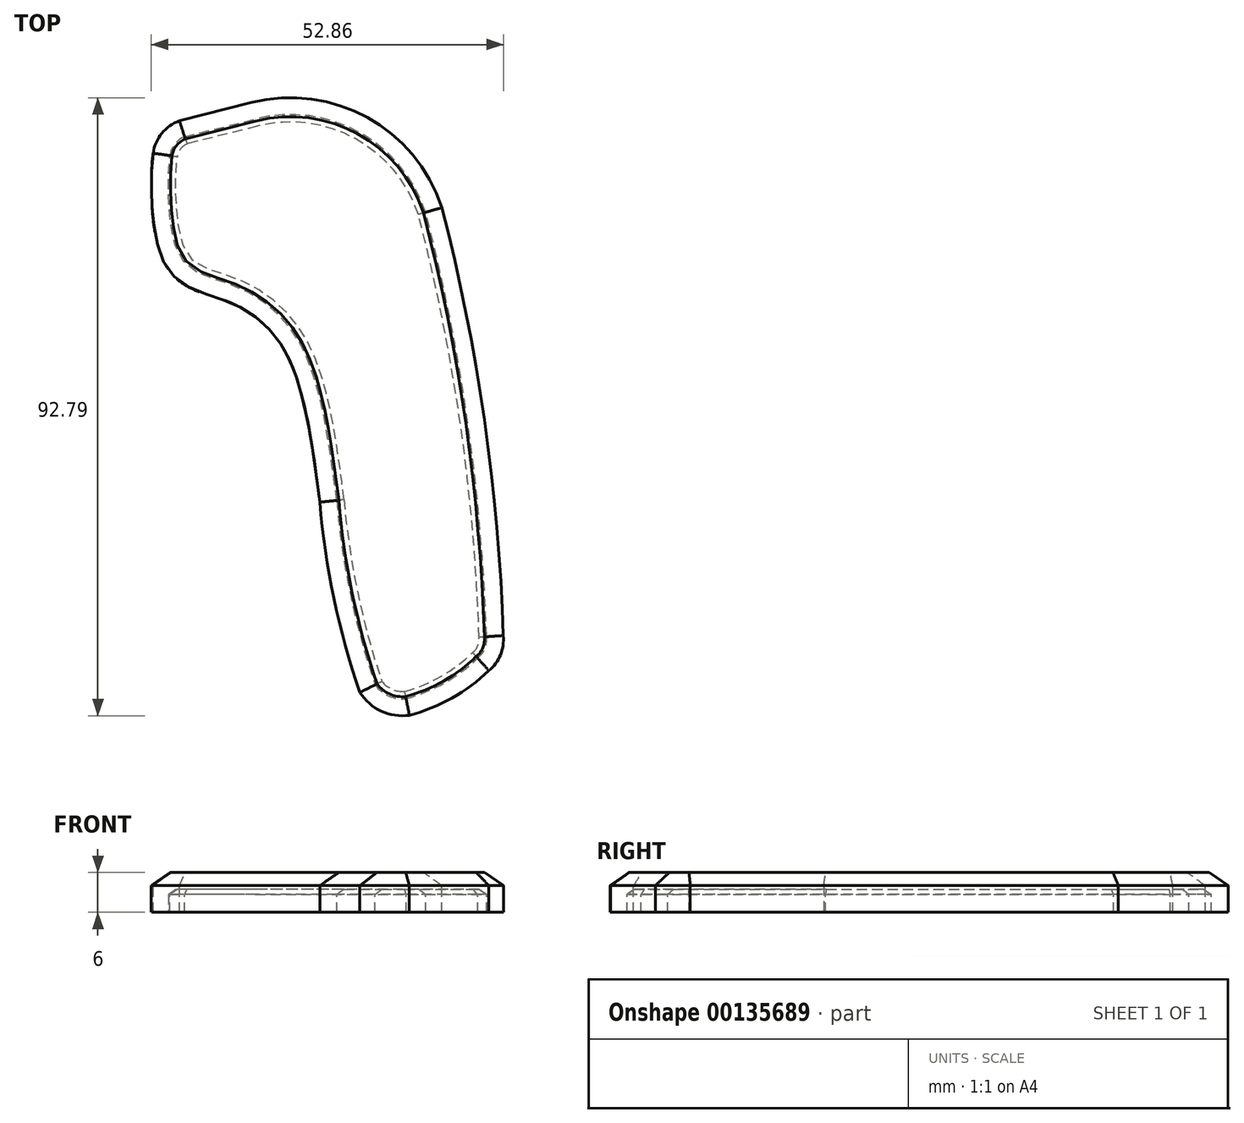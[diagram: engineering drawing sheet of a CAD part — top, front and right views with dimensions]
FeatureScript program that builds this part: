
annotation { "Feature Type Name" : "Feature", "Feature Type Description" : "" }
export const myFeature = defineFeature(function(context is Context, id is Id, definition is map)
    precondition{}
    {
        {
            var Q0;
            Q0=qCreatedBy(makeId("Top.planeOp"),FACE);
            var sketch = newSketch(context, id + "F0", { "sketchPlane" : qUnion([Q0])});
            skPoint(sketch, "E0", {"position": v(-31.69, 34.1) * mm});
            skPoint(sketch, "E1", {"position": v(-29.68, 36.64) * mm});
            skArc(sketch, "E2", {"start": v(-29.68, 36.64) * mm, "mid": v(-31.01, 35.62) * mm, "end": v(-31.69, 34.1) * mm});
            skLineSegment(sketch, "E3", {"start": v(-29.68, 36.64) * mm, "end": v(-19.1, 39.32) * mm});
            skArc(sketch, "E4", {"start": v(6.09, 25.52) * mm, "mid": v(-3.8, 37.37) * mm, "end": v(-19.1, 39.32) * mm});
            skArc(sketch, "E5", {"start": v(15.2, -38.13) * mm, "mid": v(12.4, -6.05) * mm, "end": v(6.09, 25.52) * mm});
            skArc(sketch, "E6", {"start": v(14, -41.06) * mm, "mid": v(14.98, -39.75) * mm, "end": v(15.2, -38.13) * mm});
            skArc(sketch, "E7", {"start": v(3.4, -47.09) * mm, "mid": v(9.08, -44.75) * mm, "end": v(14, -41.06) * mm});
            skPoint(sketch, "E8", {"position": v(-0.9, -45.16) * mm});
            skArc(sketch, "E9", {"start": v(-0.9, -45.16) * mm, "mid": v(1, -46.7) * mm, "end": v(3.4, -47.09) * mm});
            skArc(sketch, "E10", {"start": v(-6.64, -17.6) * mm, "mid": v(-4.61, -31.56) * mm, "end": v(-0.9, -45.16) * mm});
            skPoint(sketch, "E11", {"position": v(-21.1, 14.4) * mm});
            skPoint(sketch, "E12", {"position": v(-12.38, 6.43) * mm});
            skPoint(sketch, "E13", {"position": v(-26.85, 16.46) * mm});
            skPoint(sketch, "E14", {"position": v(-30.6, 19.98) * mm});
            skPoint(sketch, "E15", {"position": v(-31.9, 31.23) * mm});
            skFitSpline(sketch, "E16", {"points": [v(-6.64, -17.6) * mm, v(-12.38, 6.43) * mm, v(-21.1, 14.4) * mm, v(-26.85, 16.46) * mm, v(-30.6, 19.98) * mm, v(-31.9, 31.23) * mm, v(-31.69, 34.1) * mm], "startDerivative": vector(-12.9, 99.78) * mm, "endDerivative": vector(2.83, 23.45) * mm});
            skSolve(sketch);
        }
        {
            var Q0;
            Q0=makeQuery(id+"F0.imprint","IMPRINT",FACE,{"disambiguationData":[TD([[makeQuery(id+"F0.imprint","IMPRINT",EDGE,{"derivedFrom":sQuery(id+"F0.wireOp",EDGE,"E2")}),1.0]])]});
            extrude(context, id + "F1", {"entities" : qUnion([Q0]), "oppositeDirection" : true, "depth" : 2 * mm, "hasDraft" : true, "draftAngle" : 55 * degree});
        }
        {
            var Q0;
            Q0=makeQuery(id+"F1.opExtrude","CAP_FACE",FACE,{"disambiguationData":[OSD([sQuery(id+"F0.wireOp",EDGE,"E2"),sQuery(id+"F0.wireOp",EDGE,"E3"),sQuery(id+"F0.wireOp",EDGE,"E4"),sQuery(id+"F0.wireOp",EDGE,"E5"),sQuery(id+"F0.wireOp",EDGE,"E6"),sQuery(id+"F0.wireOp",EDGE,"E7"),sQuery(id+"F0.wireOp",EDGE,"E9"),sQuery(id+"F0.wireOp",EDGE,"E10"),sQuery(id+"F0.wireOp",EDGE,"E16")])],"isStart":false});
            extrude(context, id + "F2", {"entities" : qUnion([Q0]), "operationType" : NewBodyOperationType.ADD, "depth" : 4 * mm});
        }
        {
            var Q0;
            Q0=makeQuery(id+"F2.opExtrude","CAP_FACE",FACE,{"disambiguationData":[OSD([sQuery(id+"F0.wireOp",EDGE,"E2"),sQuery(id+"F0.wireOp",EDGE,"E3"),sQuery(id+"F0.wireOp",EDGE,"E4"),sQuery(id+"F0.wireOp",EDGE,"E5"),sQuery(id+"F0.wireOp",EDGE,"E6"),sQuery(id+"F0.wireOp",EDGE,"E7"),sQuery(id+"F0.wireOp",EDGE,"E9"),sQuery(id+"F0.wireOp",EDGE,"E10"),sQuery(id+"F0.wireOp",EDGE,"E16")])],"isStart":false});
            shell(context, id + "F3", {"entities" : qUnion([Q0]), "thickness" : 2.54 * mm});
        }
    });
